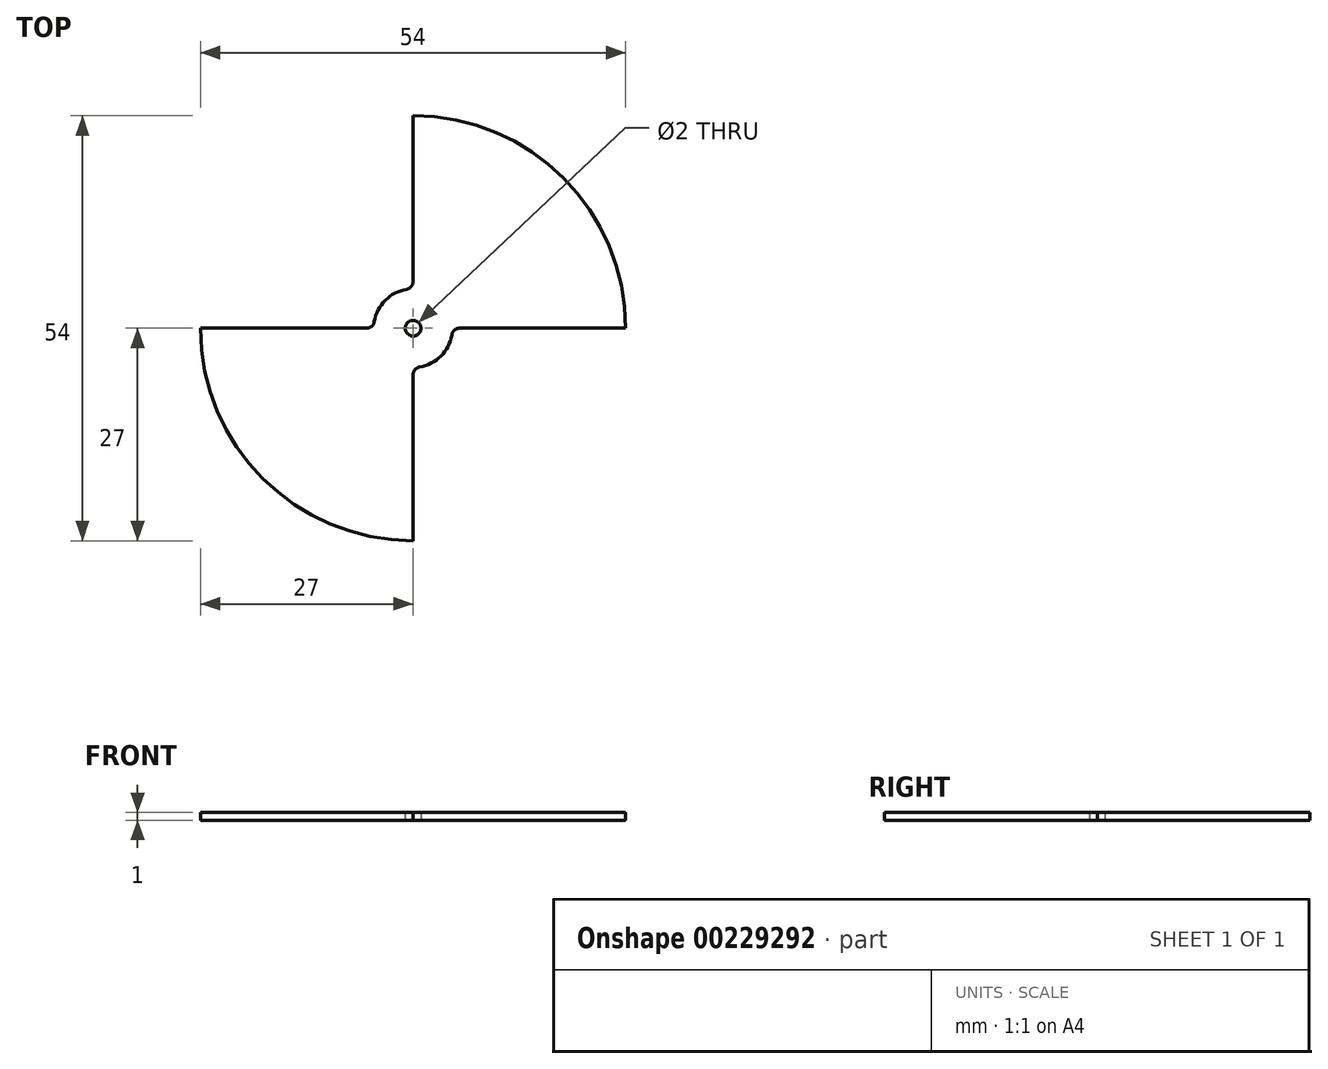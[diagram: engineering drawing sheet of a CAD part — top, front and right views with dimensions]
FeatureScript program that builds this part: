
annotation { "Feature Type Name" : "Feature", "Feature Type Description" : "" }
export const myFeature = defineFeature(function(context is Context, id is Id, definition is map)
    precondition{}
    {
        {
            var Q0;
            Q0=qCreatedBy(makeId("Top.planeOp"),FACE);
            var sketch = newSketch(context, id + "F0", { "sketchPlane" : qUnion([Q0])});
            skCircle(sketch, "E0", {"center": v(0, 0) * mm, "radius": 1 * mm});
            skArc(sketch, "E1", {"start": v(-0.83, 4.93) * mm, "mid": v(-3.54, 3.54) * mm, "end": v(-4.93, 0.83) * mm});
            skArc(sketch, "E2", {"start": v(-27, 0) * mm, "mid": v(-19.1, -19.1) * mm, "end": v(0, -27) * mm});
            skLineSegment(sketch, "E3", {"start": v(0, 27) * mm, "end": v(0, 5.92) * mm});
            skLineSegment(sketch, "E4", {"start": v(27, 0) * mm, "end": v(5.92, 0) * mm});
            skLineSegment(sketch, "E5", {"start": v(0, -27) * mm, "end": v(0, -5.92) * mm});
            skLineSegment(sketch, "E6", {"start": v(-27, 0) * mm, "end": v(-5.92, 0) * mm});
            skArc(sketch, "E7.trimOffspring", {"start": v(27, 0) * mm, "mid": v(19.1, 19.1) * mm, "end": v(0, 27) * mm});
            skArc(sketch, "E8.trimOffspring", {"start": v(0.83, -4.93) * mm, "mid": v(3.54, -3.54) * mm, "end": v(4.93, -0.83) * mm});
            skPoint(sketch, "E9.visualSharp", {"position": v(-5, 0) * mm});
            skArc(sketch, "E9.filletArc", {"start": v(-5.92, 0) * mm, "mid": v(-5.27, 0.24) * mm, "end": v(-4.93, 0.83) * mm});
            skPoint(sketch, "E10.visualSharp", {"position": v(0, 5) * mm});
            skArc(sketch, "E10.filletArc", {"start": v(-0.83, 4.93) * mm, "mid": v(-0.24, 5.27) * mm, "end": v(0, 5.92) * mm});
            skPoint(sketch, "E11.visualSharp", {"position": v(0, -5) * mm});
            skArc(sketch, "E11.filletArc", {"start": v(0.83, -4.93) * mm, "mid": v(0.24, -5.27) * mm, "end": v(0, -5.92) * mm});
            skPoint(sketch, "E12.visualSharp", {"position": v(5, 0) * mm});
            skArc(sketch, "E12.filletArc", {"start": v(5.92, 0) * mm, "mid": v(5.27, -0.24) * mm, "end": v(4.93, -0.83) * mm});
            skSolve(sketch);
        }
        {
            var Q0;
            Q0 = qSketchRegion(id + "F0", true);
            extrude(context, id + "F1", {"entities" : qUnion([Q0]), "depth" : 1 * mm});
        }
    });
